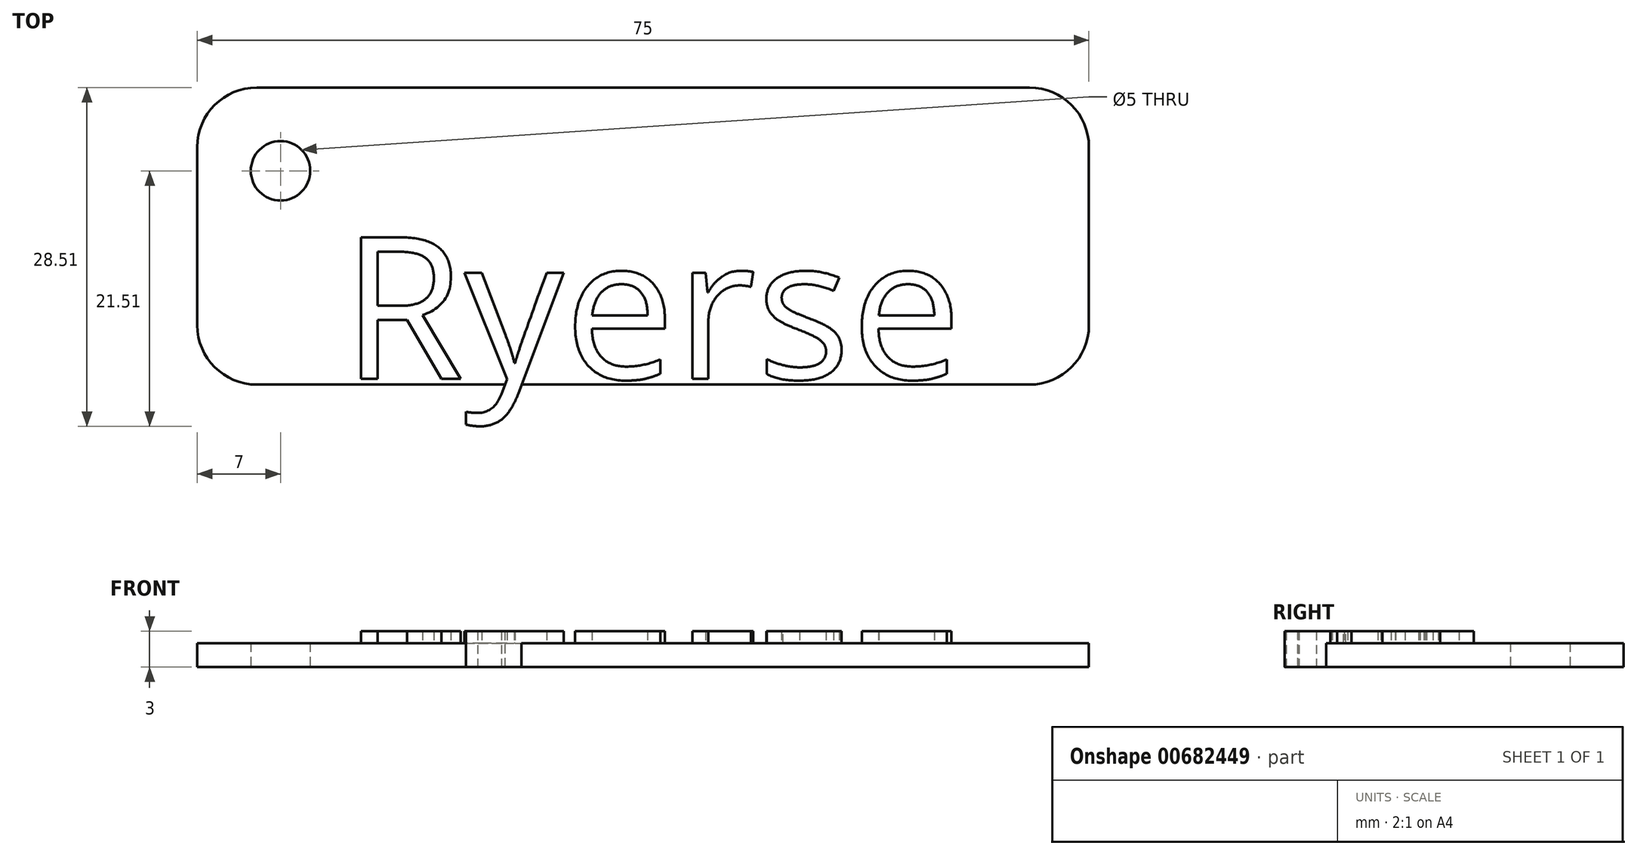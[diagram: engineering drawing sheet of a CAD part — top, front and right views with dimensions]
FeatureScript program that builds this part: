
annotation { "Feature Type Name" : "Feature", "Feature Type Description" : "" }
export const myFeature = defineFeature(function(context is Context, id is Id, definition is map)
    precondition{}
    {
        {
            var Q0;
            Q0=qCreatedBy(makeId("Top.planeOp"),FACE);
            var sketch = newSketch(context, id + "F0", { "sketchPlane" : qUnion([Q0])});
            skLineSegment(sketch, "E0.bottom", {"start": v(-32.5, 12.5) * mm, "end": v(32.5, 12.5) * mm});
            skLineSegment(sketch, "E0.top", {"start": v(-32.5, -12.5) * mm, "end": v(32.5, -12.5) * mm});
            skLineSegment(sketch, "E0.left", {"start": v(-37.5, 7.5) * mm, "end": v(-37.5, -7.5) * mm});
            skLineSegment(sketch, "E0.right", {"start": v(37.5, 7.5) * mm, "end": v(37.5, -7.5) * mm});
            skPoint(sketch, "E0.middle", {"position": v(0, 0) * mm});
            skPoint(sketch, "E1.visualSharp", {"position": v(-37.5, 12.5) * mm});
            skArc(sketch, "E1.filletArc", {"start": v(-32.5, 12.5) * mm, "mid": v(-36.04, 11.04) * mm, "end": v(-37.5, 7.5) * mm});
            skPoint(sketch, "E2.visualSharp", {"position": v(-37.5, -12.5) * mm});
            skArc(sketch, "E2.filletArc", {"start": v(-37.5, -7.5) * mm, "mid": v(-36.04, -11.04) * mm, "end": v(-32.5, -12.5) * mm});
            skPoint(sketch, "E3.visualSharp", {"position": v(37.5, -12.5) * mm});
            skArc(sketch, "E3.filletArc", {"start": v(32.5, -12.5) * mm, "mid": v(36.04, -11.04) * mm, "end": v(37.5, -7.5) * mm});
            skPoint(sketch, "E4.visualSharp", {"position": v(37.5, 12.5) * mm});
            skArc(sketch, "E4.filletArc", {"start": v(37.5, 7.5) * mm, "mid": v(36.04, 11.04) * mm, "end": v(32.5, 12.5) * mm});
            skSolve(sketch);
        }
        {
            var Q0;
            Q0 = qSketchRegion(id + "F0", true);
            extrude(context, id + "F1", {"entities" : qUnion([Q0]), "depth" : 2 * mm, "offsetDistance" : 25 * mm});
        }
        {
            var Q0;
            Q0=qCreatedBy(makeId("Top.planeOp"),FACE);
            var sketch = newSketch(context, id + "F2", { "sketchPlane" : qUnion([Q0])});
            skPoint(sketch, "E5", {"position": v(-30.5, 5.5) * mm});
            skSolve(sketch);
        }
        {
            var Q0;
            Q0=sQuery(id+"F2.wireOp",VERTEX,"E5");
            var Q1;
            Q1=makeQuery(id+"F1.opExtrude","SWEPT_BODY",BODY,{"disambiguationData":[OSD([sQuery(id+"F0.wireOp",EDGE,"E0.bottom"),sQuery(id+"F0.wireOp",EDGE,"E0.top"),sQuery(id+"F0.wireOp",EDGE,"E0.left"),sQuery(id+"F0.wireOp",EDGE,"E0.right"),sQuery(id+"F0.wireOp",EDGE,"E1.filletArc"),sQuery(id+"F0.wireOp",EDGE,"E2.filletArc"),sQuery(id+"F0.wireOp",EDGE,"E3.filletArc"),sQuery(id+"F0.wireOp",EDGE,"E4.filletArc")])]});
            hole(context, id + "F3", {"style" : HoleStyle.SIMPLE, "endStyle" : HoleEndStyle.THROUGH, "oppositeDirection" : true, "holeDiameter" : 5 * mm, "majorDiameter" : 5 * mm, "isTappedThrough" : true, "tappedDepth" : 12 * mm, "tapClearance" : 3, "locations" : qUnion([Q0]), "scope" : qUnion([Q1])});
        }
        {
            var Q0;
            Q0=qCreatedBy(makeId("Top.planeOp"),FACE);
            var sketch = newSketch(context, id + "F4", { "sketchPlane" : qUnion([Q0])});
            skText(sketch, "E6", { "text": "Ryerse", "fontName": "OpenSans-Regular.ttf"});
            const initialGuessF4  = {"E6": [-0.02535, -0.012, 1, 0, 0.012]};
            skSetInitialGuess(sketch, initialGuessF4);
            skSolve(sketch);
        }
        {
            var Q0;
            Q0 = qSketchRegion(id + "F4", true);
            extrude(context, id + "F5", {"entities" : qUnion([Q0]), "operationType" : NewBodyOperationType.ADD, "depth" : 3 * mm, "offsetDistance" : 25 * mm});
        }
    });
